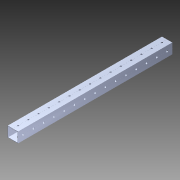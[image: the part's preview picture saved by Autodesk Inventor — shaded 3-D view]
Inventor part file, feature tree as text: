
AUTODESK INVENTOR PART (.ipt)
format: ipt  version: 2014 SP1 (Build 180222100, 222)  size: 1,156,096 bytes
history: native  units: in
note: dims shown in document units (in); Inventor stores cm internally (conversion verified against a paired STEP export)
features: pattern_circular x1, other x1, extrude x1, imported_body x1, sketch x1
ambient origin geometry x8: Origin, YZ Plane, XZ Plane, XY Plane, X Axis, Y Axis, Z Axis, Center Point
bodies: Body1 (feature_tree)
feature tree (5):
  pattern_circular  "CirPattern2"
  other  "1x1 tube1"
  extrude  "Extrusion1"  [1 undecoded]
  imported_body  "Base1"
  sketch  "Sketch1"  dims[d0=44.0in d1=0.0in]
note: 1 required parameter value undecoded (feature->parameter linkage not recoverable at this tier; creation-order binding heuristic only, values carry confidence <= 0.55)
